# Revit family: Electronics_Community-Point-Source_Biamp_Loudspeaker_V2_6
name_source: partatom
category: Communication Devices
units: mm (PartAtom-declared; Revit-internal decimal feet)

## family parameters
Cut with Voids When Loaded = No
Host = Face
Maintain Annotation Orientation = No
OmniClass Number = 23.85.10.11.14.14.14
Part Type = Normal
Room Calculation Point = No
Round Connector Dimension = Use Diameter
Shared = No

## types (4) — shared parameters
Crossover Frequency = 1.3 kHz
Default Elevation = 48 "
Depth = 10.1 "
Description = V2-6 Two-Way, Full-Range Compact Loudspeaker System
Driver Protection = DYNA-TECH protection circuitry
Drivers = LF 1 x 6.5-inch cone, HF 1 x 1-inch
Enclosure = Trapezoidal (22.5° included angle) 18mm, 11-ply cross-laminated birch
Free Standing = Free Standing
Frequency Response = 110 Hz to 16 kHz (±3 dB)
Height = 15.5 "
Input Connection = NL4-compatible locking connector with terminal strip in parallel
Loudspeaker Type = Compact two-way, full-range, trapezoidal, vented bass, user rotatable horn
Manufacturer = Biamp
Maximum Output = 112 dB SPL / 118 dB SPL (peak)
Minimum Impedance = 6 ohms @ 200 Hz
Mounting/Rigging = 9 x M6 threaded rigging fittings, 4 x M6 threaded fittings for third-party suspension products
Nominal Impedance = 8 ohms
Nominal –6dB Beamwidth = 90° H x 70° V (in vertical position)
Operating Range = 90 Hz to 18 kHz (-10 dB)
Optional Accessories = CMKIT ceiling mount kit, VB-TILT tilting bracket, VB-VY6 vertical yoke bracket, M6EYBLTKIT 6mm eyebolt kit
Product Documentation Link = https://downloads.biamp.com
Product Page URL = https://www.biamp.com
Product data url = https://www.bimobject.com
Recommended Signal Processing = 100 Hz, 24 dB/octave Butterworth high pass filter
Sensitivity (1W/1m) = 92 dB  (100 Hz to 12.5 kHz) free space
URL = https://www.biamp.com
Wall mount 0° = Wall mount 0°
Wall mount 10° = Wall mount 10°
Wall mount 20° = Wall mount 20°
Width = 9.8 "

## per-type parameters (varying)
| type | Connector Description | Grill Material | Housing Material | Mounting Material | Weight |
| V2-6 W | NL4, Terminal strip; 100W continuous, 250W program 28.3 volts RMS, 56.6 volts momentary peak | Biamp - Plastic - White(Grid) | Biamp - Plastic - White | Biamp - Metal - White | 19.70 lbf |
| V2-6 B | NL4, Terminal strip; 100W continuous, 250W program 28.3 volts RMS, 56.6 volts momentary peak | Biamp - Plastic - Black(Grid) | Biamp - Plastic - Black | Biamp - Metal - Black | 19.70 lbf |
| V2-6 BT | NL4, Terminal strip; 70V/100V applications | Biamp - Plastic - Black(Grid) | Biamp - Plastic - Black | Biamp - Metal - Black | 21.70 lbf |
| V2-6 WT | NL4, Terminal strip; 70V/100V applications | Biamp - Plastic - White(Grid) | Biamp - Plastic - White | Biamp - Metal - White | 21.70 lbf |

note: column(s) folded — value = type name in every type: Model

## geometry (parser evidence)
native form markers: Sweep x14
no freeform markers — native parametric forms only
